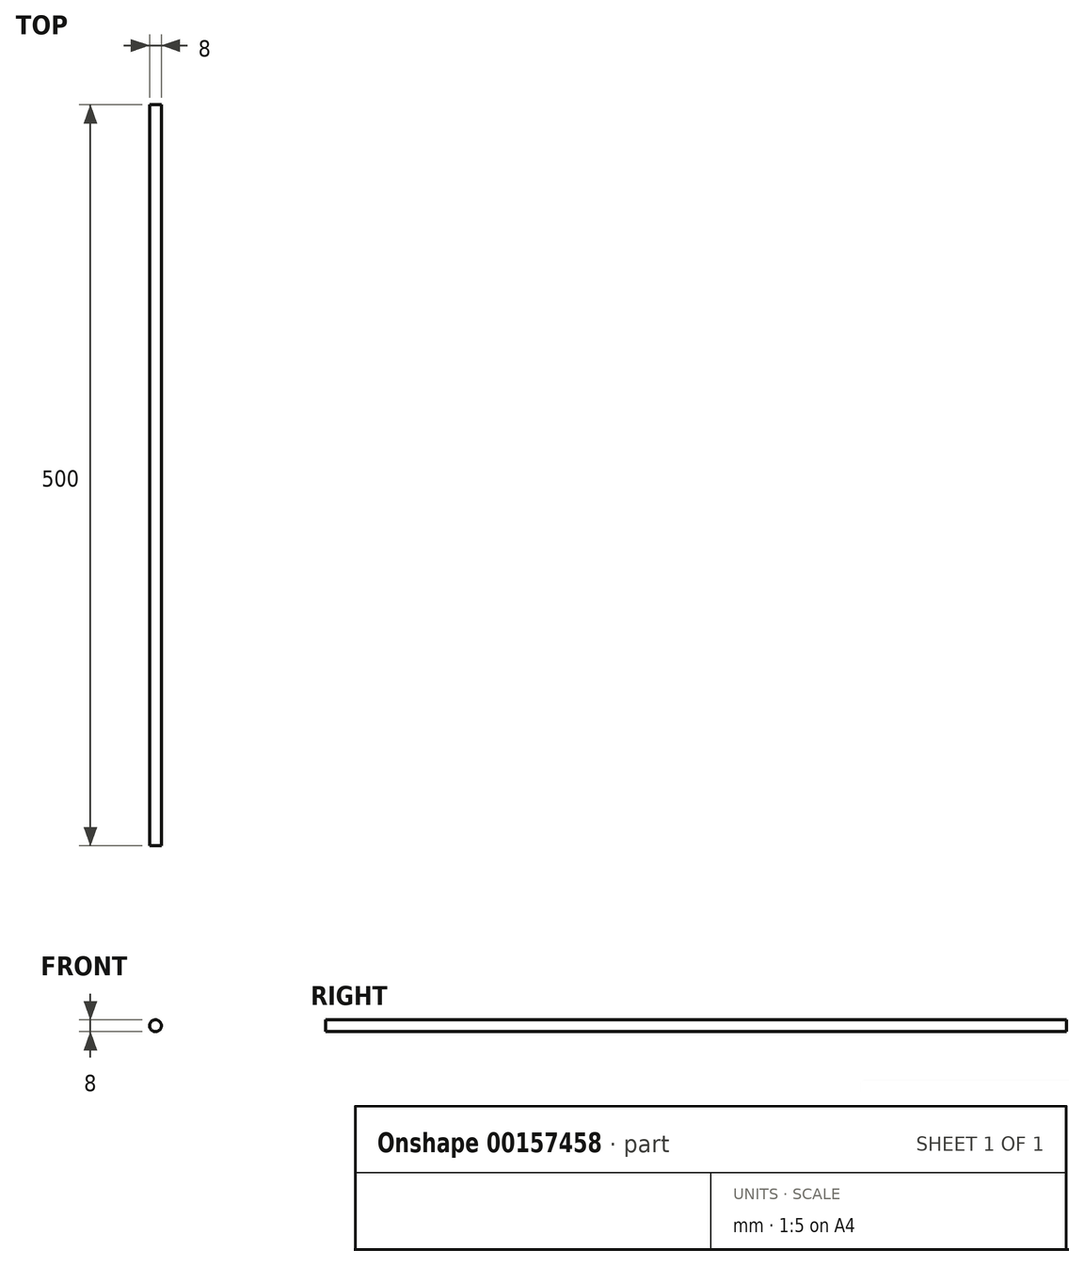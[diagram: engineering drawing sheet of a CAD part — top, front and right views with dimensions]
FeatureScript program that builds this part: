
annotation { "Feature Type Name" : "Feature", "Feature Type Description" : "" }
export const myFeature = defineFeature(function(context is Context, id is Id, definition is map)
    precondition{}
    {
        {
            var Q0;
            Q0=qCreatedBy(makeId("Front.planeOp"),FACE);
            var sketch = newSketch(context, id + "F0", { "sketchPlane" : qUnion([Q0])});
            skCircle(sketch, "E0", {"center": v(0, 0) * mm, "radius": 4 * mm});
            skSolve(sketch);
        }
        {
            var Q0;
            Q0=makeQuery(id+"F0.imprint","IMPRINT",FACE,{"disambiguationData":[TD([[makeQuery(id+"F0.imprint","IMPRINT",EDGE,{"derivedFrom":sQuery(id+"F0.wireOp",EDGE,"E0")}),1.0]])]});
            extrude(context, id + "F1", {"entities" : qUnion([Q0]), "depth" : 500 * mm});
        }
    });
